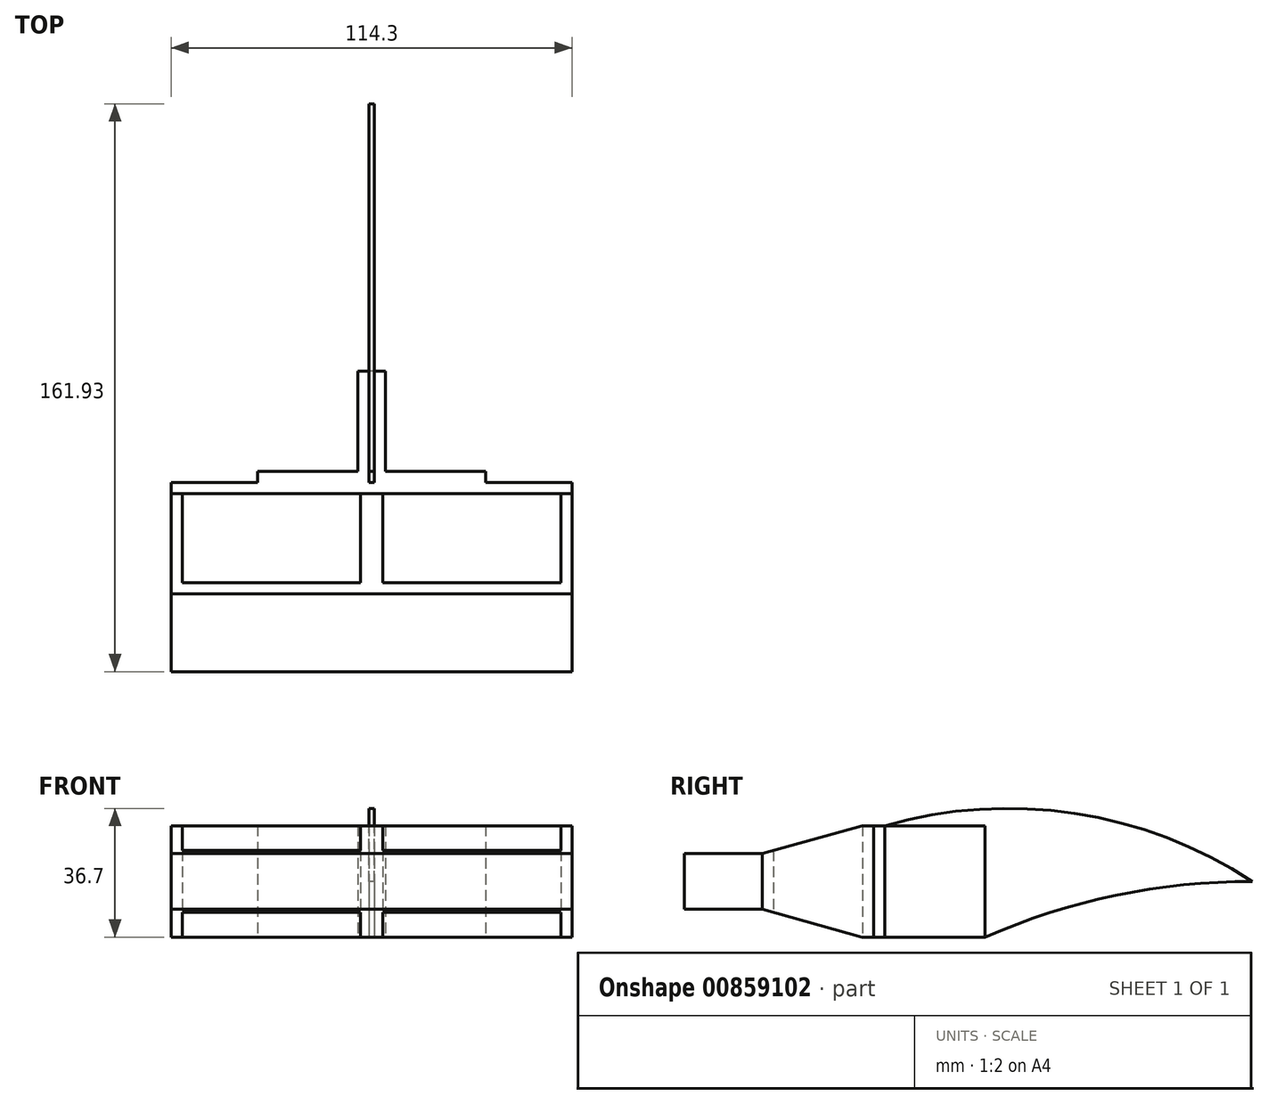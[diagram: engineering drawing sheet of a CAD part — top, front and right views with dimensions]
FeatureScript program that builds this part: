
annotation { "Feature Type Name" : "Feature", "Feature Type Description" : "" }
export const myFeature = defineFeature(function(context is Context, id is Id, definition is map)
    precondition{}
    {
        {
            var Q0;
            Q0=qCreatedBy(makeId("Top.planeOp"),FACE);
            var sketch = newSketch(context, id + "F0", { "sketchPlane" : qUnion([Q0])});
            skLineSegment(sketch, "E0.bottom", {"start": v(53.98, 0) * mm, "end": v(3.18, 0) * mm});
            skLineSegment(sketch, "E0.top", {"start": v(53.98, 25.4) * mm, "end": v(-53.98, 25.4) * mm});
            skLineSegment(sketch, "E0.left", {"start": v(53.98, 0) * mm, "end": v(53.98, 25.4) * mm});
            skLineSegment(sketch, "E0.right", {"start": v(-53.98, 0) * mm, "end": v(-53.98, 25.4) * mm});
            skPoint(sketch, "E0.middle", {"position": v(0, 12.7) * mm});
            skLineSegment(sketch, "E1.bottom", {"start": v(57.15, -3.17) * mm, "end": v(-57.15, -3.18) * mm});
            skLineSegment(sketch, "E1.top", {"start": v(57.15, 28.58) * mm, "end": v(-57.15, 28.58) * mm});
            skLineSegment(sketch, "E1.left", {"start": v(57.15, -3.17) * mm, "end": v(57.15, 28.58) * mm});
            skLineSegment(sketch, "E1.right", {"start": v(-57.15, -3.18) * mm, "end": v(-57.15, 28.58) * mm});
            skLineSegment(sketch, "E2", {"start": v(0, 0) * mm, "end": v(0, 25.4) * mm});
            skLineSegment(sketch, "E3", {"start": v(3.17, 25.4) * mm, "end": v(3.18, 0) * mm});
            skLineSegment(sketch, "E4", {"start": v(-3.18, 0) * mm, "end": v(-3.18, 25.4) * mm});
            skLineSegment(sketch, "E5.trimOffspring", {"start": v(-3.18, 0) * mm, "end": v(-53.98, 0) * mm});
            skLineSegment(sketch, "E6", {"start": v(0, 0) * mm, "end": v(0, -3.18) * mm});
            skLineSegment(sketch, "E7.bottom", {"start": v(-57.15, -3.18) * mm, "end": v(57.15, -3.18) * mm});
            skLineSegment(sketch, "E7.top", {"start": v(-57.15, -25.4) * mm, "end": v(57.15, -25.4) * mm});
            skLineSegment(sketch, "E7.left", {"start": v(-57.15, -3.18) * mm, "end": v(-57.15, -25.4) * mm});
            skLineSegment(sketch, "E7.right", {"start": v(57.15, -3.18) * mm, "end": v(57.15, -25.4) * mm});
            skLineSegment(sketch, "E8.bottom", {"start": v(0.8, 60.33) * mm, "end": v(3.97, 60.33) * mm});
            skLineSegment(sketch, "E8.top", {"start": v(0.8, 28.58) * mm, "end": v(32.54, 28.58) * mm});
            skLineSegment(sketch, "E8.left", {"start": v(0.8, 60.33) * mm, "end": v(0.8, 28.58) * mm});
            skLineSegment(sketch, "E8.right", {"start": v(32.54, 31.75) * mm, "end": v(32.54, 28.58) * mm});
            skLineSegment(sketch, "E9.bottom", {"start": v(-0.8, 60.33) * mm, "end": v(-3.97, 60.33) * mm});
            skLineSegment(sketch, "E9.top", {"start": v(-0.8, 28.58) * mm, "end": v(-32.54, 28.58) * mm});
            skLineSegment(sketch, "E9.left", {"start": v(-0.8, 60.33) * mm, "end": v(-0.8, 28.58) * mm});
            skLineSegment(sketch, "E9.right", {"start": v(-32.54, 31.75) * mm, "end": v(-32.54, 28.58) * mm});
            skLineSegment(sketch, "E10", {"start": v(3.97, 60.33) * mm, "end": v(3.97, 31.75) * mm});
            skLineSegment(sketch, "E11", {"start": v(3.97, 31.75) * mm, "end": v(32.54, 31.75) * mm});
            skLineSegment(sketch, "E12", {"start": v(-32.54, 31.75) * mm, "end": v(-3.97, 31.75) * mm});
            skLineSegment(sketch, "E13", {"start": v(-3.97, 31.75) * mm, "end": v(-3.97, 60.33) * mm});
            skSolve(sketch);
        }
        {
            var Q0;
            Q0=makeQuery(id+"F0.imprint","IMPRINT",FACE,{"disambiguationData":[TD([[makeQuery(id+"F0.imprint","IMPRINT",EDGE,{"derivedFrom":sQuery(id+"F0.wireOp",EDGE,"E0.bottom")}),1.0]])]});
            extrude(context, id + "F1", {"entities" : qUnion([Q0]), "depth" : 15.88 * mm, "offsetDistance" : 25.4 * mm, "hasSecondDirection" : true, "secondDirectionOppositeDirection" : true, "secondDirectionDepth" : 15.88 * mm});
        }
        {
            var Q0;
            Q0=makeQuery(id+"F0.imprint","IMPRINT",FACE,{"disambiguationData":[TD([[makeQuery(id+"F0.imprint","IMPRINT",EDGE,{"derivedFrom":sQuery(id+"F0.wireOp",EDGE,"E7.top")}),1.0]])]});
            extrude(context, id + "F2", {"entities" : qUnion([Q0]), "depth" : 7.95 * mm, "offsetDistance" : 25.4 * mm, "hasSecondDirection" : true, "secondDirectionOppositeDirection" : true, "secondDirectionDepth" : 7.95 * mm});
        }
        {
            var Q0;
            Q0=makeQuery(id+"F0.imprint","IMPRINT",FACE,{"disambiguationData":[TD([[makeQuery(id+"F0.imprint","IMPRINT",EDGE,{"derivedFrom":sQuery(id+"F0.wireOp",EDGE,"E9.bottom")}),1.0]])]});
            var Q1;
            Q1=makeQuery(id+"F0.imprint","IMPRINT",FACE,{"disambiguationData":[TD([[makeQuery(id+"F0.imprint","IMPRINT",EDGE,{"derivedFrom":sQuery(id+"F0.wireOp",EDGE,"E8.bottom")}),-1.0]])]});
            extrude(context, id + "F3", {"entities" : qUnion([Q0, Q1]), "operationType" : NewBodyOperationType.ADD, "depth" : 15.88 * mm, "offsetDistance" : 25.4 * mm, "hasSecondDirection" : true, "secondDirectionOppositeDirection" : true, "secondDirectionDepth" : 15.88 * mm});
        }
        {
            var Q0;
            Q0=sQuery(id+"F0.wireOp",EDGE,"E2");
            var Q1;
            Q1=sQuery(id+"F0.wireOp",EDGE,"E6");
            extrude(context, id + "F4", {"bodyType" : ToolBodyType.SURFACE, "surfaceEntities" : qUnion([Q0, Q1]), "depth" : 15.9 * mm, "offsetDistance" : 25.4 * mm, "hasSecondDirection" : true, "secondDirectionOppositeDirection" : true, "secondDirectionDepth" : 15.9 * mm});
        }
        {
            var Q0;
            Q0=makeQuery(id+"F4.opExtrude","SWEPT_BODY",BODY,{"disambiguationData":[OSD([sQuery(id+"F0.wireOp",EDGE,"E2"),sQuery(id+"F0.wireOp",EDGE,"E6")])]});
            deleteBodies(context, id + "F5", {"entities" : qUnion([Q0])});
        }
        {
            var Q0;
            Q0=qCreatedBy(makeId("Right.planeOp"),FACE);
            var sketch = newSketch(context, id + "F6", { "sketchPlane" : qUnion([Q0])});
            skLineSegment(sketch, "E14", {"start": v(-3.18, 7.95) * mm, "end": v(25.4, 15.9) * mm});
            skLineSegment(sketch, "E15", {"start": v(25.4, 15.9) * mm, "end": v(-3.18, 15.9) * mm});
            skLineSegment(sketch, "E16", {"start": v(-3.18, 15.9) * mm, "end": v(-3.17, 7.95) * mm});
            skLineSegment(sketch, "E17", {"start": v(-3.18, -7.95) * mm, "end": v(25.4, -15.9) * mm});
            skLineSegment(sketch, "E18", {"start": v(25.4, -15.9) * mm, "end": v(-3.18, -15.9) * mm});
            skLineSegment(sketch, "E19", {"start": v(-3.18, -15.9) * mm, "end": v(-3.18, -7.95) * mm});
            skSolve(sketch);
        }
        {
            var Q0;
            Q0=makeQuery(id+"F6.imprint","IMPRINT",FACE,{"disambiguationData":[TD([[makeQuery(id+"F6.imprint","IMPRINT",EDGE,{"derivedFrom":sQuery(id+"F6.wireOp",EDGE,"E17")}),-1.0]])]});
            var Q1;
            Q1=makeQuery(id+"F6.imprint","IMPRINT",FACE,{"disambiguationData":[TD([[makeQuery(id+"F6.imprint","IMPRINT",EDGE,{"derivedFrom":sQuery(id+"F6.wireOp",EDGE,"E14")}),1.0]])]});
            extrude(context, id + "F7", {"entities" : qUnion([Q0, Q1]), "operationType" : NewBodyOperationType.REMOVE, "oppositeDirection" : true, "depth" : 57.15 * mm, "offsetDistance" : 25.4 * mm, "hasSecondDirection" : true, "secondDirectionOppositeDirection" : false, "secondDirectionDepth" : 57.15 * mm});
        }
        {
            var Q0;
            Q0=qCreatedBy(makeId("Right.planeOp"),FACE);
            var sketch = newSketch(context, id + "F8", { "sketchPlane" : qUnion([Q0])});
            skPoint(sketch, "E20", {"position": v(31.75, 15.88) * mm});
            skPoint(sketch, "E21", {"position": v(31.75, -15.88) * mm});
            skPoint(sketch, "E22", {"position": v(60.33, -15.87) * mm});
            skPoint(sketch, "E23", {"position": v(60.33, 15.88) * mm});
            skArc(sketch, "E24", {"start": v(136.53, 0) * mm, "mid": v(85.87, 19.39) * mm, "end": v(31.75, 15.88) * mm});
            skArc(sketch, "E25", {"start": v(136.53, 0) * mm, "mid": v(97.6, -4.01) * mm, "end": v(60.33, -15.87) * mm});
            skLineSegment(sketch, "E26", {"start": v(-65.94, 0) * mm, "end": v(170.17, 0) * mm, "construction": true});
            skLineSegment(sketch, "E27", {"start": v(31.75, 15.88) * mm, "end": v(31.75, -15.88) * mm});
            skLineSegment(sketch, "E28", {"start": v(31.75, -15.88) * mm, "end": v(60.33, -15.88) * mm});
            skSolve(sketch);
        }
        {
            var Q0;
            Q0=makeQuery(id+"F8.imprint","IMPRINT",FACE,{"disambiguationData":[TD([[makeQuery(id+"F8.imprint","IMPRINT",EDGE,{"derivedFrom":sQuery(id+"F8.wireOp",EDGE,"E24")}),1.0]])]});
            extrude(context, id + "F9", {"entities" : qUnion([Q0]), "depth" : 0.8 * mm, "offsetDistance" : 25.4 * mm, "hasSecondDirection" : true, "secondDirectionOppositeDirection" : true, "secondDirectionDepth" : 0.8 * mm});
        }
    });
